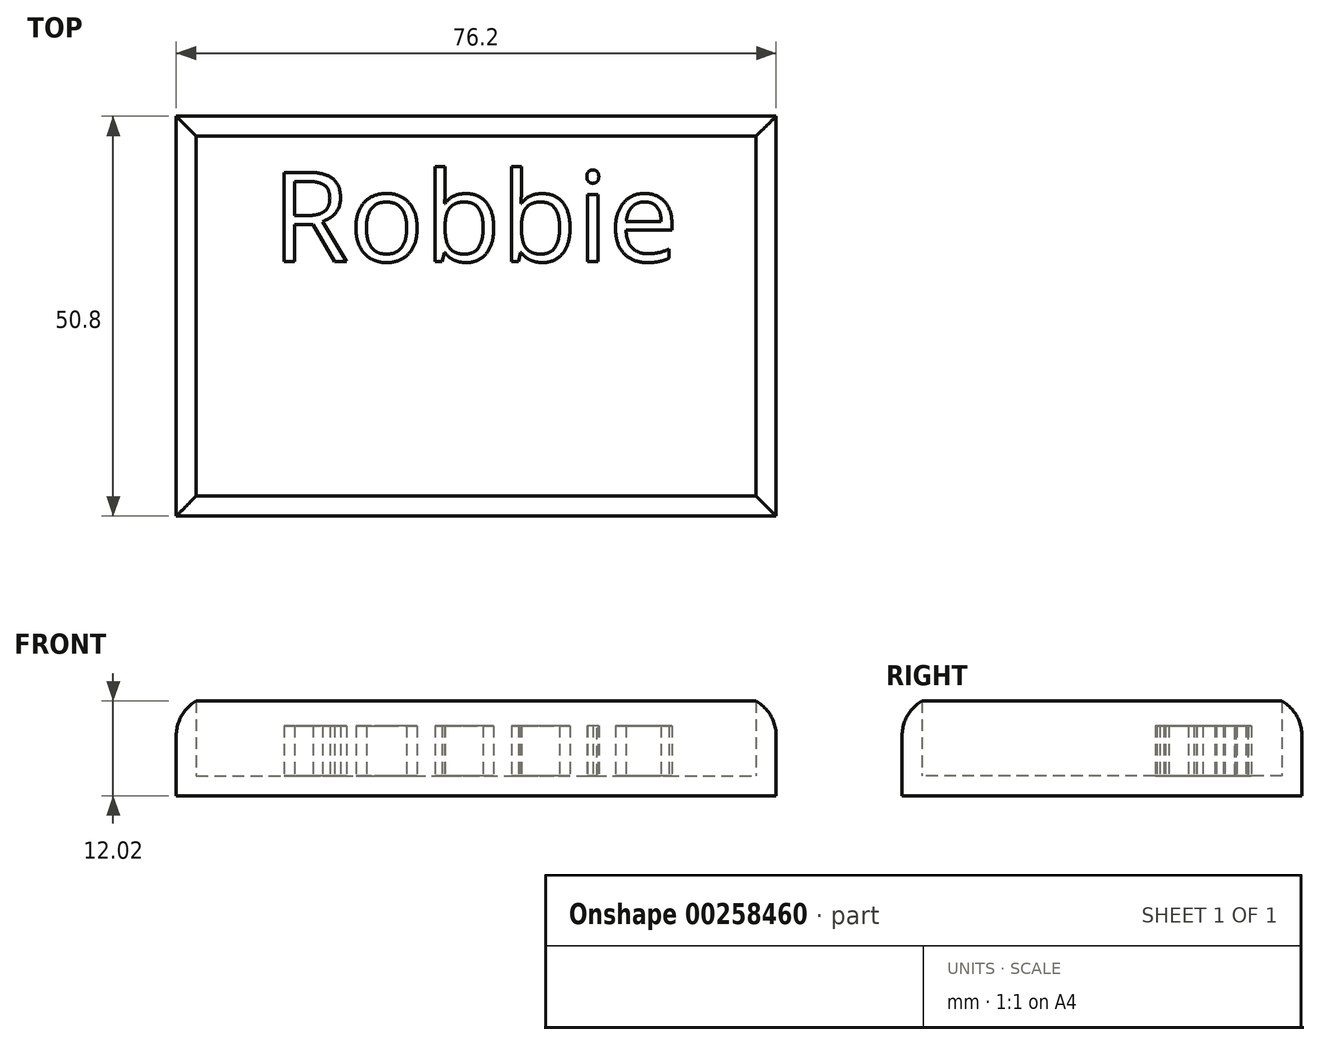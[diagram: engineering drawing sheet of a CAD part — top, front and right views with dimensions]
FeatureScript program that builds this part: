
annotation { "Feature Type Name" : "Feature", "Feature Type Description" : "" }
export const myFeature = defineFeature(function(context is Context, id is Id, definition is map)
    precondition{}
    {
        {
            var Q0;
            Q0=qCreatedBy(makeId("Top.planeOp"),FACE);
            var sketch = newSketch(context, id + "F0", { "sketchPlane" : qUnion([Q0])});
            skLineSegment(sketch, "E0.bottom", {"start": v(-34.25, 25.43) * mm, "end": v(41.95, 25.43) * mm});
            skLineSegment(sketch, "E0.top", {"start": v(-34.25, -25.37) * mm, "end": v(41.95, -25.37) * mm});
            skLineSegment(sketch, "E0.left", {"start": v(-34.25, 25.43) * mm, "end": v(-34.25, -25.37) * mm});
            skLineSegment(sketch, "E0.right", {"start": v(41.95, 25.43) * mm, "end": v(41.95, -25.37) * mm});
            skSolve(sketch);
        }
        {
            var Q0;
            Q0=makeQuery(id+"F0.imprint","IMPRINT",FACE,{"disambiguationData":[TD([[makeQuery(id+"F0.imprint","IMPRINT",EDGE,{"derivedFrom":sQuery(id+"F0.wireOp",EDGE,"E0.bottom")}),-1.0]])]});
            extrude(context, id + "F1", {"entities" : qUnion([Q0]), "depth" : 12.7 * mm});
        }
        {
            var Q0;
            Q0=makeQuery(id+"F1.opExtrude","CAP_FACE",FACE,{"disambiguationData":[OSD([sQuery(id+"F0.wireOp",EDGE,"E0.bottom"),sQuery(id+"F0.wireOp",EDGE,"E0.top"),sQuery(id+"F0.wireOp",EDGE,"E0.left"),sQuery(id+"F0.wireOp",EDGE,"E0.right")])],"isStart":false});
            shell(context, id + "F2", {"entities" : qUnion([Q0]), "thickness" : 2.54 * mm});
        }
        {
            var Q0;
            Q0=makeQuery(id+"F2.opShell","OFFSET_FACE",FACE,{"disambiguationData":[OSD([sQuery(id+"F0.wireOp",EDGE,"E0.bottom"),sQuery(id+"F0.wireOp",EDGE,"E0.top"),sQuery(id+"F0.wireOp",EDGE,"E0.left"),sQuery(id+"F0.wireOp",EDGE,"E0.right")])]});
            var sketch = newSketch(context, id + "F3", { "sketchPlane" : qUnion([Q0])});
            skText(sketch, "E1", { "text": "Robbie", "fontName": "OpenSans-Regular.ttf"});
            const initialGuessF3  = {"E1": [-0.0221, 0.00699, 1, 0, 0.0114]};
            skSetInitialGuess(sketch, initialGuessF3);
            skSolve(sketch);
        }
        {
            var Q0;
            Q0 = qSketchRegion(id + "F3", true);
            extrude(context, id + "F4", {"entities" : qUnion([Q0]), "operationType" : NewBodyOperationType.ADD, "depth" : 6.35 * mm});
        }
        {
            var Q0;
            Q0=makeQuery(id+"F1.opExtrude","CAP_EDGE",EDGE,{"disambiguationData":[OSD([sQuery(id+"F0.wireOp",EDGE,"E0.bottom")])],"isStart":false});
            var Q1;
            Q1=makeQuery(id+"F1.opExtrude","CAP_EDGE",EDGE,{"disambiguationData":[OSD([sQuery(id+"F0.wireOp",EDGE,"E0.right")])],"isStart":false});
            var Q2;
            Q2=makeQuery(id+"F1.opExtrude","CAP_EDGE",EDGE,{"disambiguationData":[OSD([sQuery(id+"F0.wireOp",EDGE,"E0.top")])],"isStart":false});
            var Q3;
            Q3=makeQuery(id+"F1.opExtrude","CAP_EDGE",EDGE,{"disambiguationData":[OSD([sQuery(id+"F0.wireOp",EDGE,"E0.left")])],"isStart":false});
            fillet(context, id + "F5", {"entities" : qUnion([Q0, Q1, Q2, Q3]), "radius" : 5.08 * mm, "tangentPropagation" : true, "allowEdgeOverflow" : false});
        }
    });
